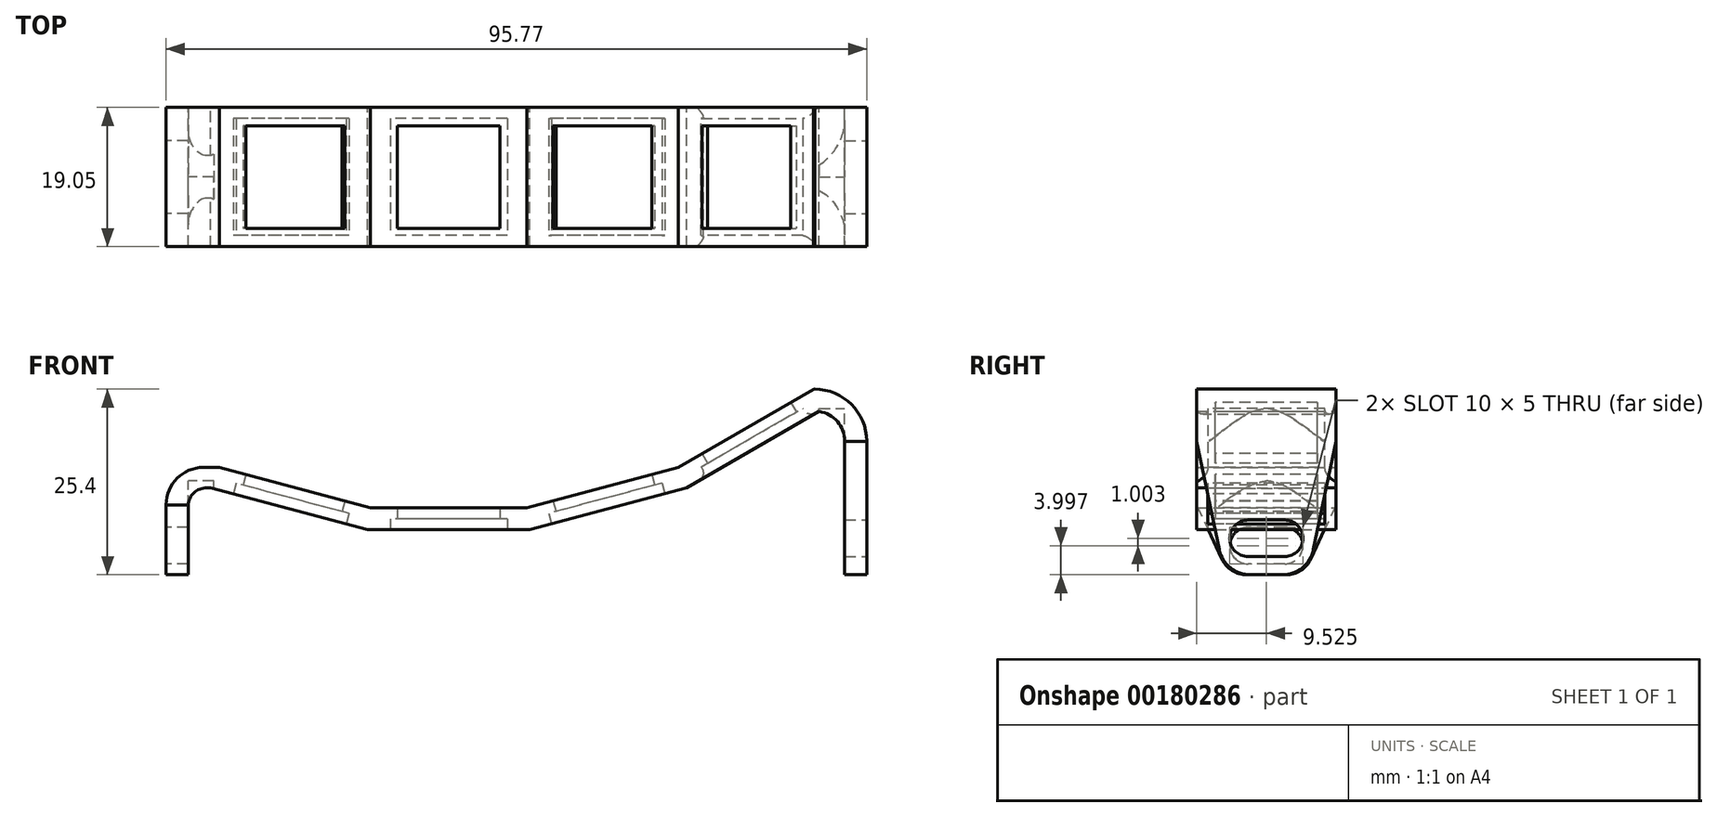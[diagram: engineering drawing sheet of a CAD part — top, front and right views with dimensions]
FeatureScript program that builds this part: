
annotation { "Feature Type Name" : "Feature", "Feature Type Description" : "" }
export const myFeature = defineFeature(function(context is Context, id is Id, definition is map)
    precondition{}
    {
        {
            var Q0;
            Q0=qCreatedBy(makeId("Front.planeOp"),FACE);
            var sketch = newSketch(context, id + "F0", { "sketchPlane" : qUnion([Q0])});
            skLineSegment(sketch, "E0.right", {"start": v(57.15, 0) * mm, "end": v(57.15, 18.29) * mm});
            skCircle(sketch, "E1.cCircle", {"center": v(0, 90.44) * mm, "radius": 81.28 * mm, "construction": true});
            skLineSegment(sketch, "E1.0", {"start": v(10.7, 9.16) * mm, "end": v(-10.7, 9.16) * mm});
            skLineSegment(sketch, "E1.1", {"start": v(-10.7, 9.16) * mm, "end": v(-31.37, 14.7) * mm});
            skLineSegment(sketch, "E1.3", {"start": v(-57.47, 32.97) * mm, "end": v(-65.04, 40.53) * mm});
            skLineSegment(sketch, "E1.4", {"start": v(-65.04, 40.53) * mm, "end": v(-75.74, 59.07) * mm});
            skLineSegment(sketch, "E1.5", {"start": v(-75.74, 59.07) * mm, "end": v(-81.28, 79.74) * mm});
            skLineSegment(sketch, "E1.6", {"start": v(-81.28, 79.74) * mm, "end": v(-81.28, 101.14) * mm});
            skLineSegment(sketch, "E1.7", {"start": v(-81.28, 101.14) * mm, "end": v(-75.74, 121.81) * mm});
            skLineSegment(sketch, "E1.8", {"start": v(-75.74, 121.81) * mm, "end": v(-65.04, 140.35) * mm});
            skLineSegment(sketch, "E1.9", {"start": v(-65.04, 140.35) * mm, "end": v(-49.9, 155.48) * mm});
            skLineSegment(sketch, "E1.10", {"start": v(-49.9, 155.48) * mm, "end": v(-31.37, 166.18) * mm});
            skLineSegment(sketch, "E1.11", {"start": v(-31.37, 166.18) * mm, "end": v(-10.7, 171.72) * mm});
            skLineSegment(sketch, "E1.12", {"start": v(-10.7, 171.72) * mm, "end": v(10.7, 171.72) * mm});
            skLineSegment(sketch, "E1.13", {"start": v(10.7, 171.72) * mm, "end": v(31.37, 166.18) * mm});
            skLineSegment(sketch, "E1.14", {"start": v(31.37, 166.18) * mm, "end": v(49.9, 155.48) * mm});
            skLineSegment(sketch, "E1.15", {"start": v(49.9, 155.48) * mm, "end": v(65.04, 140.35) * mm});
            skLineSegment(sketch, "E1.16", {"start": v(65.04, 140.35) * mm, "end": v(75.74, 121.81) * mm});
            skLineSegment(sketch, "E1.17", {"start": v(75.74, 121.81) * mm, "end": v(81.28, 101.14) * mm});
            skLineSegment(sketch, "E1.18", {"start": v(81.28, 101.14) * mm, "end": v(81.28, 79.74) * mm});
            skLineSegment(sketch, "E1.19", {"start": v(81.28, 79.74) * mm, "end": v(75.74, 59.07) * mm});
            skLineSegment(sketch, "E1.20", {"start": v(75.74, 59.07) * mm, "end": v(65.04, 40.53) * mm});
            skLineSegment(sketch, "E1.21", {"start": v(65.04, 40.53) * mm, "end": v(49.9, 25.4) * mm});
            skLineSegment(sketch, "E1.22", {"start": v(49.9, 25.4) * mm, "end": v(31.37, 14.7) * mm});
            skLineSegment(sketch, "E1.23", {"start": v(31.37, 14.7) * mm, "end": v(10.7, 9.16) * mm});
            skPoint(sketch, "E1.0.midPoint", {"position": v(0, 9.16) * mm});
            skPoint(sketch, "E2.visualSharp", {"position": v(57.15, 25.4) * mm});
            skArc(sketch, "E2.filletArc", {"start": v(57.15, 18.29) * mm, "mid": v(55.07, 23.32) * mm, "end": v(50.04, 25.4) * mm});
            skLineSegment(sketch, "E3.trimOffspring", {"start": v(49.9, 25.4) * mm, "end": v(50.04, 25.4) * mm});
            skLineSegment(sketch, "E4.3", {"start": v(-11.1, 6.16) * mm, "end": v(-32.53, 11.9) * mm});
            skLineSegment(sketch, "E4.4", {"start": v(11.1, 6.16) * mm, "end": v(-11.1, 6.16) * mm});
            skLineSegment(sketch, "E4.5", {"start": v(54.15, 0) * mm, "end": v(54.15, 18.29) * mm});
            skArc(sketch, "E4.6", {"start": v(54.15, 18.29) * mm, "mid": v(53.15, 20.98) * mm, "end": v(50.64, 22.36) * mm});
            skLineSegment(sketch, "E4.7", {"start": v(50.64, 22.36) * mm, "end": v(32.53, 11.9) * mm});
            skLineSegment(sketch, "E4.8", {"start": v(32.53, 11.9) * mm, "end": v(11.1, 6.16) * mm});
            skPoint(sketch, "E5.visualSharp", {"position": v(54.15, 0) * mm});
            skLineSegment(sketch, "E6", {"start": v(54.15, 0) * mm, "end": v(57.15, 0) * mm});
            skLineSegment(sketch, "E7", {"start": v(-31.37, 14.7) * mm, "end": v(-33.54, 14.7) * mm});
            skLineSegment(sketch, "E8", {"start": v(-38.62, 9.62) * mm, "end": v(-38.62, 0) * mm});
            skLineSegment(sketch, "E9", {"start": v(-38.62, 0) * mm, "end": v(-35.62, 0) * mm});
            skLineSegment(sketch, "E10", {"start": v(-35.62, 0) * mm, "end": v(-35.62, 9.36) * mm});
            skLineSegment(sketch, "E11", {"start": v(-33.08, 11.9) * mm, "end": v(-32.53, 11.9) * mm});
            skPoint(sketch, "E12.visualSharp", {"position": v(-38.62, 14.7) * mm});
            skArc(sketch, "E12.filletArc", {"start": v(-33.54, 14.7) * mm, "mid": v(-37.13, 13.21) * mm, "end": v(-38.62, 9.62) * mm});
            skPoint(sketch, "E13.visualSharp", {"position": v(-35.62, 11.9) * mm});
            skArc(sketch, "E13.filletArc", {"start": v(-33.08, 11.9) * mm, "mid": v(-34.87, 11.16) * mm, "end": v(-35.62, 9.36) * mm});
            skSolve(sketch);
        }
        {
            var Q0;
            Q0=makeQuery(id+"F0.imprint","IMPRINT",FACE,{"disambiguationData":[TD([[makeQuery(id+"F0.imprint","IMPRINT",EDGE,{"derivedFrom":sQuery(id+"F0.wireOp",EDGE,"E0.right")}),1.0]])]});
            extrude(context, id + "F1", {"entities" : qUnion([Q0]), "depth" : 19.05 * mm});
        }
        {
            var Q0;
            Q0=makeQuery(id+"F1.opExtrude","SWEPT_FACE",FACE,{"disambiguationData":[OSD([sQuery(id+"F0.wireOp",EDGE,"E4.7")])]});
            var sketch = newSketch(context, id + "F2", { "sketchPlane" : qUnion([Q0])});
            skLineSegment(sketch, "E14.bottom", {"start": v(38.3, 2.53) * mm, "end": v(52.3, 2.52) * mm});
            skLineSegment(sketch, "E14.top", {"start": v(38.3, 16.52) * mm, "end": v(52.3, 16.52) * mm});
            skLineSegment(sketch, "E14.left", {"start": v(38.3, 2.53) * mm, "end": v(38.3, 16.52) * mm});
            skLineSegment(sketch, "E14.right", {"start": v(52.3, 2.52) * mm, "end": v(52.3, 16.52) * mm});
            skPoint(sketch, "E14.middle", {"position": v(45.3, 9.52) * mm});
            skLineSegment(sketch, "E15.bottom", {"start": v(37.3, 1.52) * mm, "end": v(53.3, 1.52) * mm});
            skLineSegment(sketch, "E15.top", {"start": v(37.3, 17.52) * mm, "end": v(53.3, 17.52) * mm});
            skLineSegment(sketch, "E15.left", {"start": v(37.3, 1.52) * mm, "end": v(37.3, 17.52) * mm});
            skLineSegment(sketch, "E15.right", {"start": v(53.3, 1.52) * mm, "end": v(53.3, 17.52) * mm});
            skLineSegment(sketch, "E16.trimOffspring", {"start": v(45.3, 9.53) * mm, "end": v(55.03, 0) * mm, "construction": true});
            skPoint(sketch, "E17.end.orphan", {"position": v(34.12, 0) * mm});
            skSolve(sketch);
        }
        {
            var Q0;
            Q0=qSketchRegion(id+"F2",true);
            extrude(context, id + "F3", {"entities" : qUnion([Q0]), "operationType" : NewBodyOperationType.REMOVE, "oppositeDirection" : true, "depth" : 1.5 * mm});
        }
        {
            var Q0;
            Q0=makeQuery(id+"F3.boolean.opBoolean","SPLIT",FACE,{"disambiguationData":[TD([makeQuery(id+"F3.opExtrude","SWEPT_FACE",FACE,{"disambiguationData":[OSD([sQuery(id+"F2.wireOp",EDGE,"E14.bottom")])]})])],"derivedFrom":makeQuery(id+"F1.opExtrude","SWEPT_FACE",FACE,{"disambiguationData":[OSD([sQuery(id+"F0.wireOp",EDGE,"E4.7")])]})});
            extrude(context, id + "F4", {"entities" : qUnion([Q0]), "operationType" : NewBodyOperationType.REMOVE, "endBound" : BoundingType.THROUGH_ALL, "oppositeDirection" : true, "depth" : 25.4 * mm});
        }
        {
            var Q0;
            Q0=makeQuery(id+"F1.opExtrude","SWEPT_FACE",FACE,{"disambiguationData":[OSD([sQuery(id+"F0.wireOp",EDGE,"E4.8")])]});
            var sketch = newSketch(context, id + "F5", { "sketchPlane" : qUnion([Q0])});
            skLineSegment(sketch, "E18", {"start": v(12.31, 19.05) * mm, "end": v(23.4, 9.52) * mm, "construction": true});
            skLineSegment(sketch, "E19", {"start": v(34.5, 19.05) * mm, "end": v(12.31, 0) * mm, "construction": true});
            skLineSegment(sketch, "E20", {"start": v(23.4, 9.52) * mm, "end": v(34.5, 0) * mm, "construction": true});
            skLineSegment(sketch, "E21.bottom", {"start": v(31.4, 1.52) * mm, "end": v(15.4, 1.52) * mm});
            skLineSegment(sketch, "E21.top", {"start": v(31.4, 17.52) * mm, "end": v(15.4, 17.52) * mm});
            skLineSegment(sketch, "E21.left", {"start": v(31.4, 1.52) * mm, "end": v(31.4, 17.52) * mm});
            skLineSegment(sketch, "E21.right", {"start": v(15.4, 1.52) * mm, "end": v(15.4, 17.52) * mm});
            skPoint(sketch, "E21.middle", {"position": v(23.4, 9.52) * mm});
            skLineSegment(sketch, "E22.bottom", {"start": v(30.4, 2.53) * mm, "end": v(16.4, 2.52) * mm});
            skLineSegment(sketch, "E22.top", {"start": v(30.4, 16.52) * mm, "end": v(16.4, 16.52) * mm});
            skLineSegment(sketch, "E22.left", {"start": v(30.4, 2.53) * mm, "end": v(30.4, 16.52) * mm});
            skLineSegment(sketch, "E22.right", {"start": v(16.4, 2.52) * mm, "end": v(16.4, 16.52) * mm});
            skSolve(sketch);
        }
        {
            var Q0;
            Q0=qSketchRegion(id+"F5",true);
            extrude(context, id + "F6", {"entities" : qUnion([Q0]), "operationType" : NewBodyOperationType.REMOVE, "oppositeDirection" : true, "depth" : 1.5 * mm});
        }
        {
            var Q0;
            Q0=makeQuery(id+"F6.boolean.opBoolean","SPLIT",FACE,{"disambiguationData":[TD([makeQuery(id+"F6.opExtrude","SWEPT_FACE",FACE,{"disambiguationData":[OSD([sQuery(id+"F5.wireOp",EDGE,"E22.bottom")])]})])],"derivedFrom":makeQuery(id+"F1.opExtrude","SWEPT_FACE",FACE,{"disambiguationData":[OSD([sQuery(id+"F0.wireOp",EDGE,"E4.8")])]})});
            extrude(context, id + "F7", {"entities" : qUnion([Q0]), "operationType" : NewBodyOperationType.REMOVE, "endBound" : BoundingType.THROUGH_ALL, "oppositeDirection" : true, "depth" : 25.4 * mm});
        }
        {
            var Q0;
            Q0=makeQuery(id+"F1.opExtrude","SWEPT_FACE",FACE,{"disambiguationData":[OSD([sQuery(id+"F0.wireOp",EDGE,"E4.4")])]});
            var sketch = newSketch(context, id + "F8", { "sketchPlane" : qUnion([Q0])});
            skLineSegment(sketch, "E23", {"start": v(-11.1, 19.05) * mm, "end": v(0, 9.53) * mm, "construction": true});
            skLineSegment(sketch, "E24", {"start": v(11.1, 19.05) * mm, "end": v(-11.1, 0) * mm, "construction": true});
            skLineSegment(sketch, "E25", {"start": v(0, 9.53) * mm, "end": v(11.1, 0) * mm, "construction": true});
            skLineSegment(sketch, "E26.bottom", {"start": v(8, 1.53) * mm, "end": v(-8, 1.53) * mm});
            skLineSegment(sketch, "E26.top", {"start": v(8, 17.53) * mm, "end": v(-8, 17.53) * mm});
            skLineSegment(sketch, "E26.left", {"start": v(8, 1.53) * mm, "end": v(8, 17.53) * mm});
            skLineSegment(sketch, "E26.right", {"start": v(-8, 1.53) * mm, "end": v(-8, 17.53) * mm});
            skPoint(sketch, "E26.middle", {"position": v(0, 9.53) * mm});
            skLineSegment(sketch, "E27.bottom", {"start": v(7, 2.52) * mm, "end": v(-7, 2.52) * mm});
            skLineSegment(sketch, "E27.top", {"start": v(7, 16.52) * mm, "end": v(-7, 16.52) * mm});
            skLineSegment(sketch, "E27.left", {"start": v(7, 2.52) * mm, "end": v(7, 16.52) * mm});
            skLineSegment(sketch, "E27.right", {"start": v(-7, 2.52) * mm, "end": v(-7, 16.52) * mm});
            skSolve(sketch);
        }
        {
            var Q0;
            Q0=qSketchRegion(id+"F8",true);
            extrude(context, id + "F9", {"entities" : qUnion([Q0]), "operationType" : NewBodyOperationType.REMOVE, "oppositeDirection" : true, "depth" : 1.5 * mm});
        }
        {
            var Q0;
            Q0=makeQuery(id+"F9.boolean.opBoolean","SPLIT",FACE,{"disambiguationData":[TD([makeQuery(id+"F9.opExtrude","SWEPT_FACE",FACE,{"disambiguationData":[OSD([sQuery(id+"F8.wireOp",EDGE,"E27.bottom")])]})])],"derivedFrom":makeQuery(id+"F1.opExtrude","SWEPT_FACE",FACE,{"disambiguationData":[OSD([sQuery(id+"F0.wireOp",EDGE,"E4.4")])]})});
            extrude(context, id + "F10", {"entities" : qUnion([Q0]), "operationType" : NewBodyOperationType.REMOVE, "endBound" : BoundingType.THROUGH_ALL, "oppositeDirection" : true, "depth" : 25.4 * mm});
        }
        {
            var Q0;
            Q0=makeQuery(id+"F1.opExtrude","SWEPT_FACE",FACE,{"disambiguationData":[OSD([sQuery(id+"F0.wireOp",EDGE,"E4.3")])]});
            var sketch = newSketch(context, id + "F11", { "sketchPlane" : qUnion([Q0])});
            skLineSegment(sketch, "E28.bottom", {"start": v(-15.31, 1.53) * mm, "end": v(-31.31, 1.53) * mm});
            skLineSegment(sketch, "E28.top", {"start": v(-15.31, 17.53) * mm, "end": v(-31.31, 17.53) * mm});
            skLineSegment(sketch, "E28.left", {"start": v(-15.31, 1.53) * mm, "end": v(-15.31, 17.53) * mm});
            skLineSegment(sketch, "E28.right", {"start": v(-31.31, 1.53) * mm, "end": v(-31.31, 17.53) * mm});
            skPoint(sketch, "E28.middle", {"position": v(-23.31, 9.53) * mm});
            skLineSegment(sketch, "E29.bottom", {"start": v(-16.31, 2.53) * mm, "end": v(-30.31, 2.53) * mm});
            skLineSegment(sketch, "E29.top", {"start": v(-16.31, 16.53) * mm, "end": v(-30.31, 16.53) * mm});
            skLineSegment(sketch, "E29.left", {"start": v(-16.31, 2.53) * mm, "end": v(-16.31, 16.53) * mm});
            skLineSegment(sketch, "E29.right", {"start": v(-30.31, 2.53) * mm, "end": v(-30.31, 16.53) * mm});
            skSolve(sketch);
        }
        {
            var Q0;
            Q0=qSketchRegion(id+"F11",true);
            extrude(context, id + "F12", {"entities" : qUnion([Q0]), "operationType" : NewBodyOperationType.REMOVE, "oppositeDirection" : true, "depth" : 1.5 * mm});
        }
        {
            var Q0;
            Q0=makeQuery(id+"F12.boolean.opBoolean","SPLIT",FACE,{"disambiguationData":[TD([makeQuery(id+"F12.opExtrude","SWEPT_FACE",FACE,{"disambiguationData":[OSD([sQuery(id+"F11.wireOp",EDGE,"E29.bottom")])]})])],"derivedFrom":makeQuery(id+"F1.opExtrude","SWEPT_FACE",FACE,{"disambiguationData":[OSD([sQuery(id+"F0.wireOp",EDGE,"E4.3")])]})});
            extrude(context, id + "F13", {"entities" : qUnion([Q0]), "operationType" : NewBodyOperationType.REMOVE, "endBound" : BoundingType.THROUGH_ALL, "oppositeDirection" : true, "depth" : 25.4 * mm});
        }
        {
            var Q0;
            Q0=makeQuery(id+"F3.boolean.opBoolean","COPY",EDGE,{"derivedFrom":makeQuery(id+"F3.opExtrude","CAP_EDGE",EDGE,{"disambiguationData":[OSD([sQuery(id+"F2.wireOp",EDGE,"E15.right")])],"isStart":true})});
            var Q1;
            Q1=makeQuery(id+"F3.boolean.opBoolean","COPY",EDGE,{"derivedFrom":makeQuery(id+"F3.opExtrude","CAP_EDGE",EDGE,{"disambiguationData":[OSD([sQuery(id+"F2.wireOp",EDGE,"E15.top")])],"isStart":true})});
            var Q2;
            Q2=makeQuery(id+"F3.boolean.opBoolean","COPY",EDGE,{"derivedFrom":makeQuery(id+"F3.opExtrude","CAP_EDGE",EDGE,{"disambiguationData":[OSD([sQuery(id+"F2.wireOp",EDGE,"E15.left")])],"isStart":true})});
            var Q3;
            Q3=makeQuery(id+"F3.boolean.opBoolean","COPY",EDGE,{"derivedFrom":makeQuery(id+"F3.opExtrude","CAP_EDGE",EDGE,{"disambiguationData":[OSD([sQuery(id+"F2.wireOp",EDGE,"E15.bottom")])],"isStart":true})});
            var Q4;
            Q4=makeQuery(id+"F6.boolean.opBoolean","COPY",EDGE,{"derivedFrom":makeQuery(id+"F6.opExtrude","CAP_EDGE",EDGE,{"disambiguationData":[OSD([sQuery(id+"F5.wireOp",EDGE,"E21.bottom")])],"isStart":true})});
            var Q5;
            Q5=makeQuery(id+"F6.boolean.opBoolean","COPY",EDGE,{"derivedFrom":makeQuery(id+"F6.opExtrude","CAP_EDGE",EDGE,{"disambiguationData":[OSD([sQuery(id+"F5.wireOp",EDGE,"E21.left")])],"isStart":true})});
            var Q6;
            Q6=makeQuery(id+"F6.boolean.opBoolean","COPY",EDGE,{"derivedFrom":makeQuery(id+"F6.opExtrude","CAP_EDGE",EDGE,{"disambiguationData":[OSD([sQuery(id+"F5.wireOp",EDGE,"E21.top")])],"isStart":true})});
            var Q7;
            Q7=makeQuery(id+"F6.boolean.opBoolean","COPY",EDGE,{"derivedFrom":makeQuery(id+"F6.opExtrude","CAP_EDGE",EDGE,{"disambiguationData":[OSD([sQuery(id+"F5.wireOp",EDGE,"E21.right")])],"isStart":true})});
            var Q8;
            Q8=makeQuery(id+"F9.boolean.opBoolean","COPY",EDGE,{"derivedFrom":makeQuery(id+"F9.opExtrude","CAP_EDGE",EDGE,{"disambiguationData":[OSD([sQuery(id+"F8.wireOp",EDGE,"E26.left")])],"isStart":true})});
            var Q9;
            Q9=makeQuery(id+"F9.boolean.opBoolean","COPY",EDGE,{"derivedFrom":makeQuery(id+"F9.opExtrude","CAP_EDGE",EDGE,{"disambiguationData":[OSD([sQuery(id+"F8.wireOp",EDGE,"E26.top")])],"isStart":true})});
            var Q10;
            Q10=makeQuery(id+"F9.boolean.opBoolean","COPY",EDGE,{"derivedFrom":makeQuery(id+"F9.opExtrude","CAP_EDGE",EDGE,{"disambiguationData":[OSD([sQuery(id+"F8.wireOp",EDGE,"E26.right")])],"isStart":true})});
            var Q11;
            Q11=makeQuery(id+"F9.boolean.opBoolean","COPY",EDGE,{"derivedFrom":makeQuery(id+"F9.opExtrude","CAP_EDGE",EDGE,{"disambiguationData":[OSD([sQuery(id+"F8.wireOp",EDGE,"E26.bottom")])],"isStart":true})});
            var Q12;
            Q12=makeQuery(id+"F12.boolean.opBoolean","COPY",EDGE,{"derivedFrom":makeQuery(id+"F12.opExtrude","CAP_EDGE",EDGE,{"disambiguationData":[OSD([sQuery(id+"F11.wireOp",EDGE,"E28.left")])],"isStart":true})});
            var Q13;
            Q13=makeQuery(id+"F12.boolean.opBoolean","COPY",EDGE,{"derivedFrom":makeQuery(id+"F12.opExtrude","CAP_EDGE",EDGE,{"disambiguationData":[OSD([sQuery(id+"F11.wireOp",EDGE,"E28.top")])],"isStart":true})});
            var Q14;
            Q14=makeQuery(id+"F12.boolean.opBoolean","COPY",EDGE,{"derivedFrom":makeQuery(id+"F12.opExtrude","CAP_EDGE",EDGE,{"disambiguationData":[OSD([sQuery(id+"F11.wireOp",EDGE,"E28.bottom")])],"isStart":true})});
            var Q15;
            Q15=makeQuery(id+"F12.boolean.opBoolean","COPY",EDGE,{"derivedFrom":makeQuery(id+"F12.opExtrude","CAP_EDGE",EDGE,{"disambiguationData":[OSD([sQuery(id+"F11.wireOp",EDGE,"E28.right")])],"isStart":true})});
            var Q16;
            Q16=makeQuery(id+"FImuVpmlFVpr7mz_1.boolean.opBoolean","COPY",EDGE,{"derivedFrom":makeQuery(id+"FImuVpmlFVpr7mz_1.opExtrude","CAP_EDGE",EDGE,{"disambiguationData":[OSD([sQuery(id+"Fs7CY0uaLBf5hhG_1.wireOp",EDGE,"bVJm5sH4-SQKF-Oii1-7mGO-BevqyFC5kFCD.left")])],"isStart":true})});
            var Q17;
            Q17=makeQuery(id+"FImuVpmlFVpr7mz_1.boolean.opBoolean","COPY",EDGE,{"derivedFrom":makeQuery(id+"FImuVpmlFVpr7mz_1.opExtrude","CAP_EDGE",EDGE,{"disambiguationData":[OSD([sQuery(id+"Fs7CY0uaLBf5hhG_1.wireOp",EDGE,"bVJm5sH4-SQKF-Oii1-7mGO-BevqyFC5kFCD.top")])],"isStart":true})});
            var Q18;
            Q18=makeQuery(id+"FImuVpmlFVpr7mz_1.boolean.opBoolean","COPY",EDGE,{"derivedFrom":makeQuery(id+"FImuVpmlFVpr7mz_1.opExtrude","CAP_EDGE",EDGE,{"disambiguationData":[OSD([sQuery(id+"Fs7CY0uaLBf5hhG_1.wireOp",EDGE,"bVJm5sH4-SQKF-Oii1-7mGO-BevqyFC5kFCD.bottom")])],"isStart":true})});
            var Q19;
            Q19=makeQuery(id+"FImuVpmlFVpr7mz_1.boolean.opBoolean","COPY",EDGE,{"derivedFrom":makeQuery(id+"FImuVpmlFVpr7mz_1.opExtrude","CAP_EDGE",EDGE,{"disambiguationData":[OSD([sQuery(id+"Fs7CY0uaLBf5hhG_1.wireOp",EDGE,"bVJm5sH4-SQKF-Oii1-7mGO-BevqyFC5kFCD.right")])],"isStart":true})});
            fillet(context, id + "F14", {"entities" : qUnion([Q0, Q1, Q2, Q3, Q4, Q5, Q6, Q7, Q8, Q9, Q10, Q11, Q12, Q13, Q14, Q15, Q16, Q17, Q18, Q19]), "radius" : 1.5 * mm, "tangentPropagation" : true, "rho" : 0.5, "crossSection" : FilletCrossSection.CONIC, "allowEdgeOverflow" : false});
        }
        {
            var Q0;
            Q0=makeQuery(id+"F1.opExtrude","SWEPT_FACE",FACE,{"disambiguationData":[OSD([sQuery(id+"F0.wireOp",EDGE,"E0.right")])]});
            var sketch = newSketch(context, id + "F15", { "sketchPlane" : qUnion([Q0])});
            skLineSegment(sketch, "E30", {"start": v(-19.05, 18.29) * mm, "end": v(-9.53, 9.14) * mm, "construction": true});
            skLineSegment(sketch, "E31", {"start": v(0, 18.29) * mm, "end": v(-19.05, 0) * mm, "construction": true});
            skLineSegment(sketch, "E32", {"start": v(-9.53, 9.14) * mm, "end": v(0, 0) * mm, "construction": true});
            skLineSegment(sketch, "E33", {"start": v(-9.53, 9.14) * mm, "end": v(-9.53, 0) * mm, "construction": true});
            skLineSegment(sketch, "E34", {"start": v(-9.53, 5) * mm, "end": v(-7.03, 5) * mm});
            skLineSegment(sketch, "E35", {"start": v(-9.53, 5) * mm, "end": v(-12.03, 5) * mm});
            skArc(sketch, "E36.0.endCap", {"start": v(-7.03, 7.5) * mm, "mid": v(-4.53, 5) * mm, "end": v(-7.03, 2.5) * mm});
            skLineSegment(sketch, "E36.0.left", {"start": v(-12.03, 7.5) * mm, "end": v(-7.03, 7.5) * mm});
            skLineSegment(sketch, "E36.0.right", {"start": v(-12.03, 2.5) * mm, "end": v(-7.03, 2.5) * mm});
            skArc(sketch, "E36.1.endCap", {"start": v(-12.03, 2.5) * mm, "mid": v(-14.53, 5) * mm, "end": v(-12.03, 7.5) * mm});
            skLineSegment(sketch, "E36.1.left", {"start": v(-7.03, 2.5) * mm, "end": v(-12.03, 2.5) * mm});
            skLineSegment(sketch, "E36.1.right", {"start": v(-7.03, 7.5) * mm, "end": v(-12.03, 7.5) * mm});
            skSolve(sketch);
        }
        {
            var Q0;
            Q0=makeQuery(id+"F1.opExtrude","CAP_EDGE",EDGE,{"disambiguationData":[OSD([sQuery(id+"F0.wireOp",EDGE,"MSP6JUtO-vGIJ-oiNa-KPMo-hUFYFk3M8dIk")])],"isStart":false});
            var Q1;
            Q1=makeQuery(id+"F1.opExtrude","CAP_EDGE",EDGE,{"disambiguationData":[OSD([sQuery(id+"F0.wireOp",EDGE,"MSP6JUtO-vGIJ-oiNa-KPMo-hUFYFk3M8dIk")])],"isStart":true});
            var Q2;
            Q2=makeQuery(id+"F1.opExtrude","CAP_EDGE",EDGE,{"disambiguationData":[OSD([sQuery(id+"F0.wireOp",EDGE,"E6")])],"isStart":false});
            chamfer(context, id + "F16", {"entities" : qUnion([Q0, Q1, Q2]), "chamferType" : ChamferType.OFFSET_ANGLE, "width" : 3.8 * mm, "oppositeDirection" : true, "angle" : 78.2 * degree, "tangentPropagation" : true});
        }
        {
            var Q0;
            Q0=qSketchRegion(id+"F15",true);
            extrude(context, id + "F17", {"entities" : qUnion([Q0]), "operationType" : NewBodyOperationType.REMOVE, "endBound" : BoundingType.UP_TO_NEXT, "oppositeDirection" : true, "depth" : 25.4 * mm});
        }
        {
            var Q0;
            Q0=makeQuery(id+"F1.opExtrude","CAP_EDGE",EDGE,{"disambiguationData":[OSD([sQuery(id+"F0.wireOp",EDGE,"E6")])],"isStart":true});
            chamfer(context, id + "F18", {"entities" : qUnion([Q0]), "chamferType" : ChamferType.OFFSET_ANGLE, "width" : 3.8 * mm, "oppositeDirection" : false, "angle" : 78.2 * degree, "tangentPropagation" : true});
        }
        {
            var Q0;
            {var subQ0=sQuery(id+"F0.wireOp",EDGE,"MSP6JUtO-vGIJ-oiNa-KPMo-hUFYFk3M8dIk");Q0=makeQuery(id+"F16.opChamfer","BLEND_EDGE",EDGE,{"blendedFrom":[makeQuery(id+"F1.opExtrude","CAP_EDGE",EDGE,{"disambiguationData":[OSD([subQ0])],"isStart":false}),makeQuery(id+"F1.opExtrude","SWEPT_FACE",FACE,{"disambiguationData":[OSD([subQ0])]})],"blendedInto":[makeQuery(id+"F1.opExtrude","SWEPT_FACE",FACE,{"disambiguationData":[OSD([subQ0])]})]});}
            var Q1;
            {var subQ0=sQuery(id+"F0.wireOp",EDGE,"MSP6JUtO-vGIJ-oiNa-KPMo-hUFYFk3M8dIk");Q1=makeQuery(id+"F16.opChamfer","BLEND_EDGE",EDGE,{"blendedFrom":[makeQuery(id+"F1.opExtrude","CAP_EDGE",EDGE,{"disambiguationData":[OSD([subQ0])],"isStart":true}),makeQuery(id+"F1.opExtrude","SWEPT_FACE",FACE,{"disambiguationData":[OSD([subQ0])]})],"blendedInto":[makeQuery(id+"F1.opExtrude","SWEPT_FACE",FACE,{"disambiguationData":[OSD([subQ0])]})]});}
            var Q2;
            {var subQ0=sQuery(id+"F0.wireOp",EDGE,"E6");Q2=makeQuery(id+"F18.opChamfer","BLEND_EDGE",EDGE,{"blendedFrom":[makeQuery(id+"F1.opExtrude","CAP_EDGE",EDGE,{"disambiguationData":[OSD([subQ0])],"isStart":true}),makeQuery(id+"F1.opExtrude","SWEPT_FACE",FACE,{"disambiguationData":[OSD([subQ0])]})],"blendedInto":[makeQuery(id+"F1.opExtrude","SWEPT_FACE",FACE,{"disambiguationData":[OSD([subQ0])]})]});}
            var Q3;
            {var subQ0=sQuery(id+"F0.wireOp",EDGE,"E6");Q3=makeQuery(id+"F16.opChamfer","BLEND_EDGE",EDGE,{"blendedFrom":[makeQuery(id+"F1.opExtrude","CAP_EDGE",EDGE,{"disambiguationData":[OSD([subQ0])],"isStart":false}),makeQuery(id+"F1.opExtrude","SWEPT_FACE",FACE,{"disambiguationData":[OSD([subQ0])]})],"blendedInto":[makeQuery(id+"F1.opExtrude","SWEPT_FACE",FACE,{"disambiguationData":[OSD([subQ0])]})]});}
            fillet(context, id + "F19", {"entities" : qUnion([Q0, Q1, Q2, Q3]), "radius" : 4.32 * mm, "tangentPropagation" : true, "allowEdgeOverflow" : false});
        }
        {
            var Q0;
            Q0=makeQuery(id+"F1.opExtrude","SWEPT_FACE",FACE,{"disambiguationData":[OSD([sQuery(id+"F0.wireOp",EDGE,"E1.1")])]});
            var sketch = newSketch(context, id + "F20", { "sketchPlane" : qUnion([Q0])});
            skLineSegment(sketch, "E37", {"start": v(-30.31, -9.53) * mm, "end": v(-16.31, -9.53) * mm, "construction": true});
            skLineSegment(sketch, "E38", {"start": v(-23.31, -16.53) * mm, "end": v(-23.31, -2.53) * mm, "construction": true});
            skSolve(sketch);
        }
        {
            var Q0;
            Q0=makeQuery(id+"F1.opExtrude","SWEPT_FACE",FACE,{"disambiguationData":[OSD([sQuery(id+"F0.wireOp",EDGE,"E1.0")])]});
            var sketch = newSketch(context, id + "F21", { "sketchPlane" : qUnion([Q0])});
            skLineSegment(sketch, "E39", {"start": v(-7, -9.52) * mm, "end": v(7, -9.52) * mm, "construction": true});
            skLineSegment(sketch, "E40", {"start": v(0, -2.52) * mm, "end": v(0, -16.52) * mm, "construction": true});
            skSolve(sketch);
        }
        {
            var Q0;
            Q0=makeQuery(id+"F1.opExtrude","SWEPT_FACE",FACE,{"disambiguationData":[OSD([sQuery(id+"F0.wireOp",EDGE,"E1.23")])]});
            var sketch = newSketch(context, id + "F22", { "sketchPlane" : qUnion([Q0])});
            skLineSegment(sketch, "E41", {"start": v(16.4, -9.53) * mm, "end": v(30.4, -9.53) * mm, "construction": true});
            skLineSegment(sketch, "E42", {"start": v(23.4, -16.52) * mm, "end": v(23.4, -2.53) * mm, "construction": true});
            skSolve(sketch);
        }
        {
            var Q0;
            Q0=makeQuery(id+"F1.opExtrude","SWEPT_FACE",FACE,{"disambiguationData":[OSD([sQuery(id+"F0.wireOp",EDGE,"E1.22")])]});
            var sketch = newSketch(context, id + "F23", { "sketchPlane" : qUnion([Q0])});
            skLineSegment(sketch, "E43", {"start": v(38.3, -9.52) * mm, "end": v(52.3, -9.52) * mm, "construction": true});
            skLineSegment(sketch, "E44", {"start": v(45.3, -16.52) * mm, "end": v(45.3, -2.52) * mm, "construction": true});
            skSolve(sketch);
        }
        {
            var Q0;
            Q0=makeQuery(id+"F1.opExtrude","SWEPT_FACE",FACE,{"disambiguationData":[OSD([sQuery(id+"F0.wireOp",EDGE,"E4.5")])]});
            var sketch = newSketch(context, id + "F24", { "sketchPlane" : qUnion([Q0])});
            skCircle(sketch, "E45", {"center": v(9.52, 18.29) * mm, "radius": 4.5 * mm, "construction": true});
            skLineSegment(sketch, "E46", {"start": v(9.52, 18.29) * mm, "end": v(9.52, 22.79) * mm, "construction": true});
            skLineSegment(sketch, "E47", {"start": v(9.52, 22.79) * mm, "end": v(1.73, 18.29) * mm, "construction": true});
            skFitSpline(sketch, "E48", {"points": [v(1.73, 18.29) * mm, v(6.96, 21.98) * mm, v(9.52, 22.79) * mm], "startDerivative": vector(9.25, 7.32) * mm, "endDerivative": vector(6.11, 1.25) * mm});
            skLineSegment(sketch, "E49", {"start": v(9.52, 22.79) * mm, "end": v(17.32, 18.29) * mm, "construction": true});
            skFitSpline(sketch, "E50", {"points": [v(17.32, 18.29) * mm, v(11.8, 22.17) * mm, v(9.52, 22.79) * mm], "startDerivative": vector(-9.62, 7.6) * mm, "endDerivative": vector(-5.62, 0.82) * mm});
            skLineSegment(sketch, "E51", {"start": v(1.73, 18.29) * mm, "end": v(17.32, 18.29) * mm});
            skSolve(sketch);
        }
        {
            var Q0;
            Q0=qSketchRegion(id+"F24",true);
            extrude(context, id + "F25", {"entities" : qUnion([Q0]), "operationType" : NewBodyOperationType.REMOVE, "depth" : 3.5 * mm});
        }
        {
            var Q0;
            Q0=makeQuery(id+"F1.opExtrude","SWEPT_FACE",FACE,{"disambiguationData":[OSD([sQuery(id+"F0.wireOp",EDGE,"E8")])]});
            var sketch = newSketch(context, id + "F26", { "sketchPlane" : qUnion([Q0])});
            skLineSegment(sketch, "E52", {"start": v(9.53, 9.62) * mm, "end": v(9.53, 0) * mm, "construction": true});
            skLineSegment(sketch, "E53", {"start": v(7.03, 4) * mm, "end": v(12.03, 4) * mm, "construction": true});
            skArc(sketch, "E54.0.startCap", {"start": v(7.03, 1.5) * mm, "mid": v(4.53, 4) * mm, "end": v(7.03, 6.5) * mm});
            skArc(sketch, "E54.0.endCap", {"start": v(12.03, 6.5) * mm, "mid": v(14.53, 4) * mm, "end": v(12.03, 1.5) * mm});
            skLineSegment(sketch, "E54.0.left", {"start": v(7.03, 6.5) * mm, "end": v(12.03, 6.5) * mm});
            skLineSegment(sketch, "E54.0.right", {"start": v(7.03, 1.5) * mm, "end": v(12.03, 1.5) * mm});
            skSolve(sketch);
        }
        {
            var Q0;
            Q0 = qSketchRegion(id + "F26", true);
            extrude(context, id + "F27", {"entities" : qUnion([Q0]), "operationType" : NewBodyOperationType.REMOVE, "endBound" : BoundingType.UP_TO_NEXT, "oppositeDirection" : true, "depth" : 25.4 * mm});
        }
        {
            var Q0;
            Q0=makeQuery(id+"F1.opExtrude","SWEPT_FACE",FACE,{"disambiguationData":[OSD([sQuery(id+"F0.wireOp",EDGE,"E10")])]});
            var sketch = newSketch(context, id + "F28", { "sketchPlane" : qUnion([Q0])});
            skCircle(sketch, "E55", {"center": v(-9.53, 8.36) * mm, "radius": 4.5 * mm, "construction": true});
            skLineSegment(sketch, "E56", {"start": v(-9.53, 8.36) * mm, "end": v(-9.53, 12.86) * mm, "construction": true});
            skLineSegment(sketch, "E57", {"start": v(-9.53, 12.86) * mm, "end": v(-17.32, 8.36) * mm, "construction": true});
            skFitSpline(sketch, "E58", {"points": [v(-17.32, 8.36) * mm, v(-12.1, 12.06) * mm, v(-9.53, 12.86) * mm], "startDerivative": vector(9.25, 7.32) * mm, "endDerivative": vector(6.11, 1.25) * mm});
            skLineSegment(sketch, "E59", {"start": v(-9.53, 12.86) * mm, "end": v(-1.73, 8.36) * mm, "construction": true});
            skFitSpline(sketch, "E60", {"points": [v(-1.73, 8.36) * mm, v(-7.25, 12.25) * mm, v(-9.53, 12.86) * mm], "startDerivative": vector(-9.62, 7.6) * mm, "endDerivative": vector(-5.62, 0.82) * mm});
            skLineSegment(sketch, "E61", {"start": v(-17.32, 8.36) * mm, "end": v(-1.73, 8.36) * mm});
            skSolve(sketch);
        }
        {
            var Q0;
            Q0 = qSketchRegion(id + "F28", true);
            extrude(context, id + "F29", {"entities" : qUnion([Q0]), "operationType" : NewBodyOperationType.REMOVE, "depth" : 3.5 * mm});
        }
        {
            var Q0;
            Q0=makeQuery(id+"F1.opExtrude","CAP_EDGE",EDGE,{"disambiguationData":[OSD([sQuery(id+"F0.wireOp",EDGE,"E9")])],"isStart":false});
            var Q1;
            Q1=makeQuery(id+"F1.opExtrude","CAP_EDGE",EDGE,{"disambiguationData":[OSD([sQuery(id+"F0.wireOp",EDGE,"E9")])],"isStart":true});
            chamfer(context, id + "F30", {"entities" : qUnion([Q0, Q1]), "chamferType" : ChamferType.OFFSET_ANGLE, "width" : 4.44 * mm, "oppositeDirection" : true, "angle" : 65 * degree, "tangentPropagation" : true});
        }
        {
            var Q0;
            {var subQ0=sQuery(id+"F0.wireOp",EDGE,"E9");Q0=makeQuery(id+"F30.opChamfer","BLEND_EDGE",EDGE,{"blendedFrom":[makeQuery(id+"F1.opExtrude","CAP_EDGE",EDGE,{"disambiguationData":[OSD([subQ0])],"isStart":false}),makeQuery(id+"F1.opExtrude","SWEPT_FACE",FACE,{"disambiguationData":[OSD([subQ0])]})],"blendedInto":[makeQuery(id+"F1.opExtrude","SWEPT_FACE",FACE,{"disambiguationData":[OSD([subQ0])]})]});}
            var Q1;
            {var subQ0=sQuery(id+"F0.wireOp",EDGE,"E9");Q1=makeQuery(id+"F30.opChamfer","BLEND_EDGE",EDGE,{"blendedFrom":[makeQuery(id+"F1.opExtrude","CAP_EDGE",EDGE,{"disambiguationData":[OSD([subQ0])],"isStart":true}),makeQuery(id+"F1.opExtrude","SWEPT_FACE",FACE,{"disambiguationData":[OSD([subQ0])]})],"blendedInto":[makeQuery(id+"F1.opExtrude","SWEPT_FACE",FACE,{"disambiguationData":[OSD([subQ0])]})]});}
            fillet(context, id + "F31", {"entities" : qUnion([Q0, Q1]), "radius" : 3.8 * mm, "tangentPropagation" : true, "allowEdgeOverflow" : false});
        }
        {
            var Q0;
            Q0=makeQuery(id+"F29.boolean.opBoolean","MERGE",FACE,{"derivedFrom":[makeQuery(id+"F1.opExtrude","SWEPT_FACE",FACE,{"disambiguationData":[OSD([sQuery(id+"F0.wireOp",EDGE,"E10")])]}),makeQuery(id+"F29.opExtrude","CAP_FACE",FACE,{"disambiguationData":[OSD([sQuery(id+"F28.wireOp",EDGE,"E58"),sQuery(id+"F28.wireOp",EDGE,"E60"),sQuery(id+"F28.wireOp",EDGE,"E61")])],"isStart":true})]});
            var sketch = newSketch(context, id + "F32", { "sketchPlane" : qUnion([Q0])});
            skLineSegment(sketch, "E62", {"start": v(-9.53, 6.5) * mm, "end": v(-9.53, 1.5) * mm, "construction": true});
            skSolve(sketch);
        }
        {
            var Q0;
            Q0=makeQuery(id+"F2.imprint","IMPRINT",FACE,{"disambiguationData":[TD([[makeQuery(id+"F2.imprint","IMPRINT",EDGE,{"derivedFrom":sQuery(id+"F2.wireOp",EDGE,"E14.bottom")}),1.0]])]});
            extrude(context, id + "F33", {"entities" : qUnion([Q0]), "operationType" : NewBodyOperationType.REMOVE, "endBound" : BoundingType.THROUGH_ALL, "oppositeDirection" : true, "depth" : 25.4 * mm});
        }
    });
